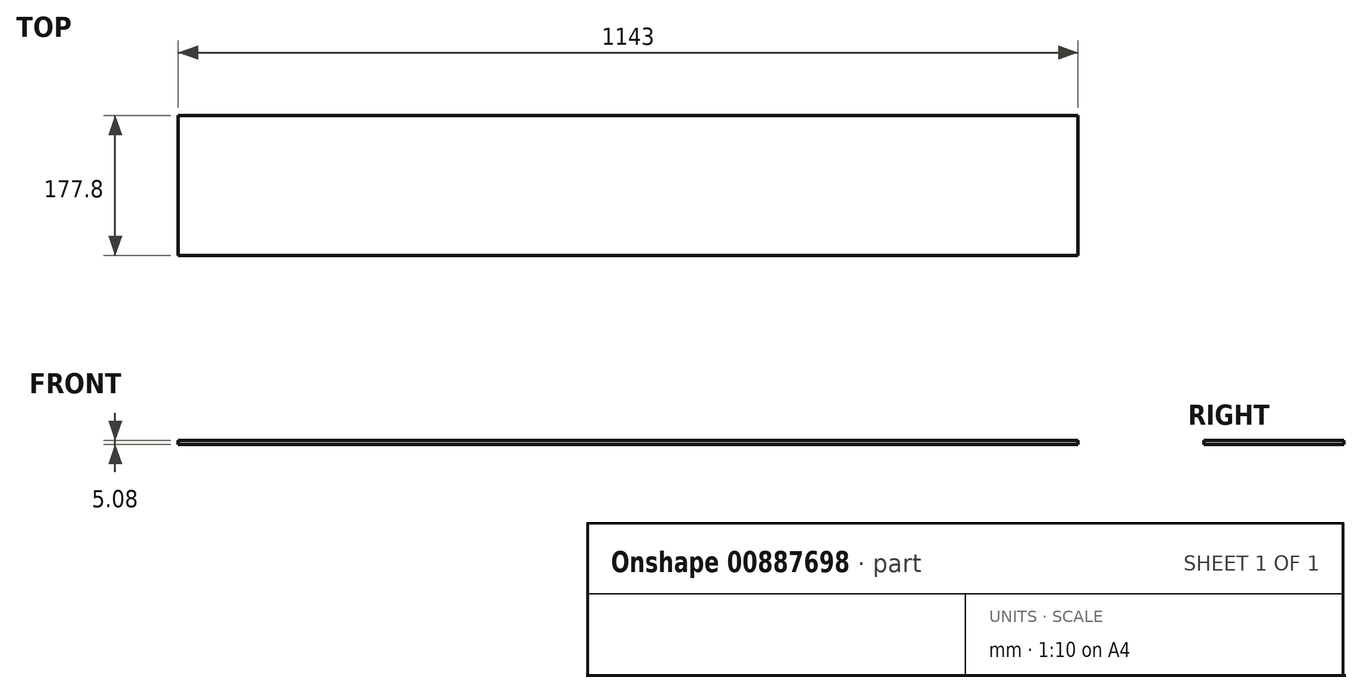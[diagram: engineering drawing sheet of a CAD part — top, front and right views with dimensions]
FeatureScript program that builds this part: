
annotation { "Feature Type Name" : "Feature", "Feature Type Description" : "" }
export const myFeature = defineFeature(function(context is Context, id is Id, definition is map)
    precondition{}
    {
        {
            var Q0;
            Q0=qCreatedBy(makeId("Top.planeOp"),FACE);
            var sketch = newSketch(context, id + "F0", { "sketchPlane" : qUnion([Q0])});
            skLineSegment(sketch, "E0.bottom", {"start": v(-571.5, 88.9) * mm, "end": v(571.5, 88.9) * mm});
            skLineSegment(sketch, "E0.top", {"start": v(-571.5, -88.9) * mm, "end": v(571.5, -88.9) * mm});
            skLineSegment(sketch, "E0.left", {"start": v(-571.5, 88.9) * mm, "end": v(-571.5, -88.9) * mm});
            skLineSegment(sketch, "E0.right", {"start": v(571.5, 88.9) * mm, "end": v(571.5, -88.9) * mm});
            skPoint(sketch, "E0.middle", {"position": v(0, 0) * mm});
            skSolve(sketch);
        }
        {
            var Q0;
            Q0=makeQuery(id+"F0.imprint","IMPRINT",FACE,{"disambiguationData":[TD([[makeQuery(id+"F0.imprint","IMPRINT",EDGE,{"derivedFrom":sQuery(id+"F0.wireOp",EDGE,"E0.bottom")}),-1.0]])]});
            extrude(context, id + "F1", {"entities" : qUnion([Q0]), "depth" : 5.08 * mm, "offsetDistance" : 25.4 * mm});
        }
    });
